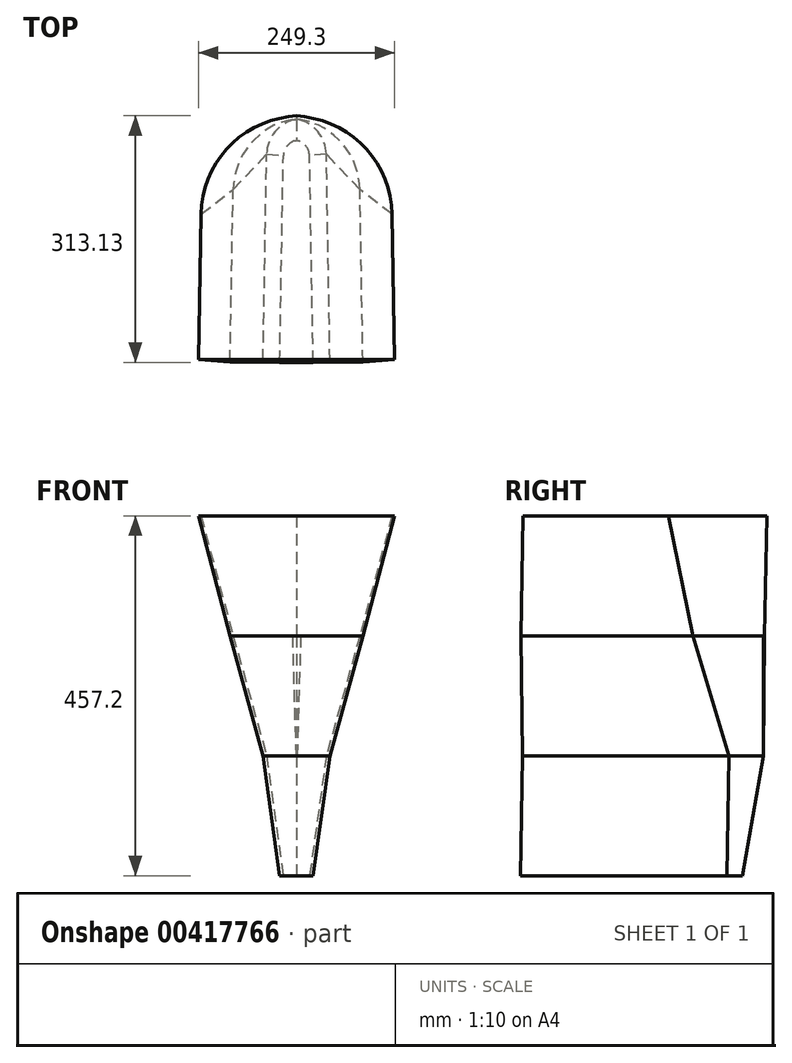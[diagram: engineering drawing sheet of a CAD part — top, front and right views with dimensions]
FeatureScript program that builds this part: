
annotation { "Feature Type Name" : "Feature", "Feature Type Description" : "" }
export const myFeature = defineFeature(function(context is Context, id is Id, definition is map)
    precondition{}
    {
        {
            var Q0;
            Q0=qCreatedBy(makeId("Top.planeOp"),FACE);
            cPlane(context, id + "F0", {"entities" : qUnion([Q0]), "cplaneType" : CPlaneType.OFFSET, "offset" : 304.8 * mm, "width" : 152.4 * mm, "height" : 152.4 * mm});
        }
        {
            var Q0;
            Q0=qCreatedBy(makeId("Top.planeOp"),FACE);
            cPlane(context, id + "F1", {"entities" : qUnion([Q0]), "cplaneType" : CPlaneType.OFFSET, "offset" : 152.4 * mm, "width" : 152.4 * mm, "height" : 152.4 * mm});
        }
        {
            var Q0;
            Q0=qCreatedBy(makeId("Top.planeOp"),FACE);
            cPlane(context, id + "F2", {"entities" : qUnion([Q0]), "cplaneType" : CPlaneType.OFFSET, "offset" : 152.4 * mm, "oppositeDirection" : true, "width" : 152.4 * mm, "height" : 152.4 * mm});
        }
        {
            var Q0;
            Q0=qCreatedBy(id+"F0.planeOp",FACE);
            var sketch = newSketch(context, id + "F3", { "sketchPlane" : qUnion([Q0])});
            skLineSegment(sketch, "E0", {"start": v(124.65, -192.9) * mm, "end": v(121.42, -8.1) * mm});
            skLineSegment(sketch, "E1", {"start": v(-124.65, -192.9) * mm, "end": v(-121.42, -8.1) * mm});
            skLineSegment(sketch, "E2", {"start": v(10.37, 115.68) * mm, "end": v(0, 117) * mm});
            skLineSegment(sketch, "E3", {"start": v(-10.37, 115.68) * mm, "end": v(0, 117) * mm});
            skArc(sketch, "E4", {"start": v(-10.37, 115.68) * mm, "mid": v(-88.97, 74.5) * mm, "end": v(-121.42, -8.1) * mm});
            skArc(sketch, "E5", {"start": v(121.42, -8.1) * mm, "mid": v(88.97, 74.5) * mm, "end": v(10.37, 115.68) * mm});
            skLineSegment(sketch, "E6", {"start": v(-124.65, -192.9) * mm, "end": v(124.65, -192.9) * mm});
            skSolve(sketch);
        }
        {
            var Q0;
            Q0=qCreatedBy(id+"F1.planeOp",FACE);
            var sketch = newSketch(context, id + "F4", { "sketchPlane" : qUnion([Q0])});
            skLineSegment(sketch, "E7", {"start": v(84.37, -195.53) * mm, "end": v(80.56, 23.03) * mm});
            skLineSegment(sketch, "E8", {"start": v(-84.37, -195.53) * mm, "end": v(-80.56, 23.03) * mm});
            skLineSegment(sketch, "E9", {"start": v(-5.35, 112.45) * mm, "end": v(0, 113.48) * mm});
            skLineSegment(sketch, "E10", {"start": v(0, 113.48) * mm, "end": v(5.35, 112.45) * mm});
            skArc(sketch, "E11", {"start": v(80.56, 23.03) * mm, "mid": v(58.81, 81.08) * mm, "end": v(5.35, 112.45) * mm});
            skArc(sketch, "E12", {"start": v(-5.35, 112.45) * mm, "mid": v(-58.81, 81.08) * mm, "end": v(-80.56, 23.03) * mm});
            skLineSegment(sketch, "E13", {"start": v(-84.37, -195.53) * mm, "end": v(84.37, -195.53) * mm});
            skSolve(sketch);
        }
        {
            var Q0;
            Q0=qCreatedBy(makeId("Top.planeOp"),FACE);
            var sketch = newSketch(context, id + "F5", { "sketchPlane" : qUnion([Q0])});
            skLineSegment(sketch, "E14", {"start": v(-0.84, 112.4) * mm, "end": v(0, 112.56) * mm});
            skLineSegment(sketch, "E15", {"start": v(0.84, 112.4) * mm, "end": v(0, 112.56) * mm});
            skLineSegment(sketch, "E16", {"start": v(42.5, -194) * mm, "end": v(37.93, 68.3) * mm});
            skLineSegment(sketch, "E17", {"start": v(-42.5, -194) * mm, "end": v(-37.93, 68.3) * mm});
            skArc(sketch, "E18", {"start": v(-0.84, 112.4) * mm, "mid": v(-27.2, 96.93) * mm, "end": v(-37.93, 68.3) * mm});
            skArc(sketch, "E19", {"start": v(37.93, 68.3) * mm, "mid": v(27.2, 96.93) * mm, "end": v(0.84, 112.4) * mm});
            skLineSegment(sketch, "E20", {"start": v(-42.5, -194) * mm, "end": v(42.5, -194) * mm});
            skSolve(sketch);
        }
        {
            var Q0;
            Q0=qCreatedBy(id+"F2.planeOp",FACE);
            var sketch = newSketch(context, id + "F6", { "sketchPlane" : qUnion([Q0])});
            skLineSegment(sketch, "E21", {"start": v(-21.33, -196.14) * mm, "end": v(-16.75, 66.16) * mm});
            skLineSegment(sketch, "E22", {"start": v(21.18, -196.14) * mm, "end": v(16.6, 66.16) * mm});
            skArc(sketch, "E23", {"start": v(-0.44, 85.55) * mm, "mid": v(-12.03, 78.75) * mm, "end": v(-16.75, 66.16) * mm});
            skArc(sketch, "E24", {"start": v(16.6, 66.16) * mm, "mid": v(11.89, 78.75) * mm, "end": v(0.3, 85.55) * mm});
            skLineSegment(sketch, "E25", {"start": v(-0.44, 85.55) * mm, "end": v(-0.06, 85.62) * mm});
            skLineSegment(sketch, "E26", {"start": v(0.3, 85.55) * mm, "end": v(-0.06, 85.62) * mm});
            skLineSegment(sketch, "E27", {"start": v(-21.33, -196.14) * mm, "end": v(21.18, -196.14) * mm});
            skSolve(sketch);
        }
        {
            var Q0;
            Q0 = qSketchRegion(id + "F3", true);
            var Q1;
            Q1 = qSketchRegion(id + "F4", true);
            var Q2;
            Q2=sQuery(id+"F4.wireOp",VERTEX,"E13.start");
            var Q3;
            Q3=sQuery(id+"F3.wireOp",VERTEX,"E6.start");
            loft(context, id + "F7", {"sheetProfilesArray" : [{ "sheetProfileEntities" : qUnion([Q0]) }, { "sheetProfileEntities" : qUnion([Q1]) }], "matchConnections" : true, "connections" : [{ "connectionEntities" : qUnion([Q2, Q3]), "connectionEdgeQueries" : qUnion([]), "connectionEdgeParameters" : [] }]});
        }
        {
            var Q0;
            Q0 = qSketchRegion(id + "F4", true);
            var Q1;
            Q1 = qSketchRegion(id + "F5", true);
            var Q2;
            Q2=sQuery(id+"F5.wireOp",VERTEX,"E20.start");
            var Q3;
            Q3=sQuery(id+"F4.wireOp",VERTEX,"E13.start");
            loft(context, id + "F8", {"sheetProfilesArray" : [{ "sheetProfileEntities" : qUnion([Q0]) }, { "sheetProfileEntities" : qUnion([Q1]) }], "matchConnections" : true, "connections" : [{ "connectionEntities" : qUnion([Q2, Q3]), "connectionEdgeQueries" : qUnion([]), "connectionEdgeParameters" : [] }]});
        }
        {
            var Q0;
            Q0 = qSketchRegion(id + "F5", true);
            var Q1;
            Q1 = qSketchRegion(id + "F6", true);
            var Q2;
            Q2=sQuery(id+"F5.wireOp",VERTEX,"E16.start");
            var Q3;
            Q3=sQuery(id+"F6.wireOp",VERTEX,"E22.start");
            loft(context, id + "F9", {"sheetProfilesArray" : [{ "sheetProfileEntities" : qUnion([Q0]) }, { "sheetProfileEntities" : qUnion([Q1]) }], "matchConnections" : true, "connections" : [{ "connectionEntities" : qUnion([Q2, Q3]), "connectionEdgeQueries" : qUnion([]), "connectionEdgeParameters" : [] }]});
        }
    });
